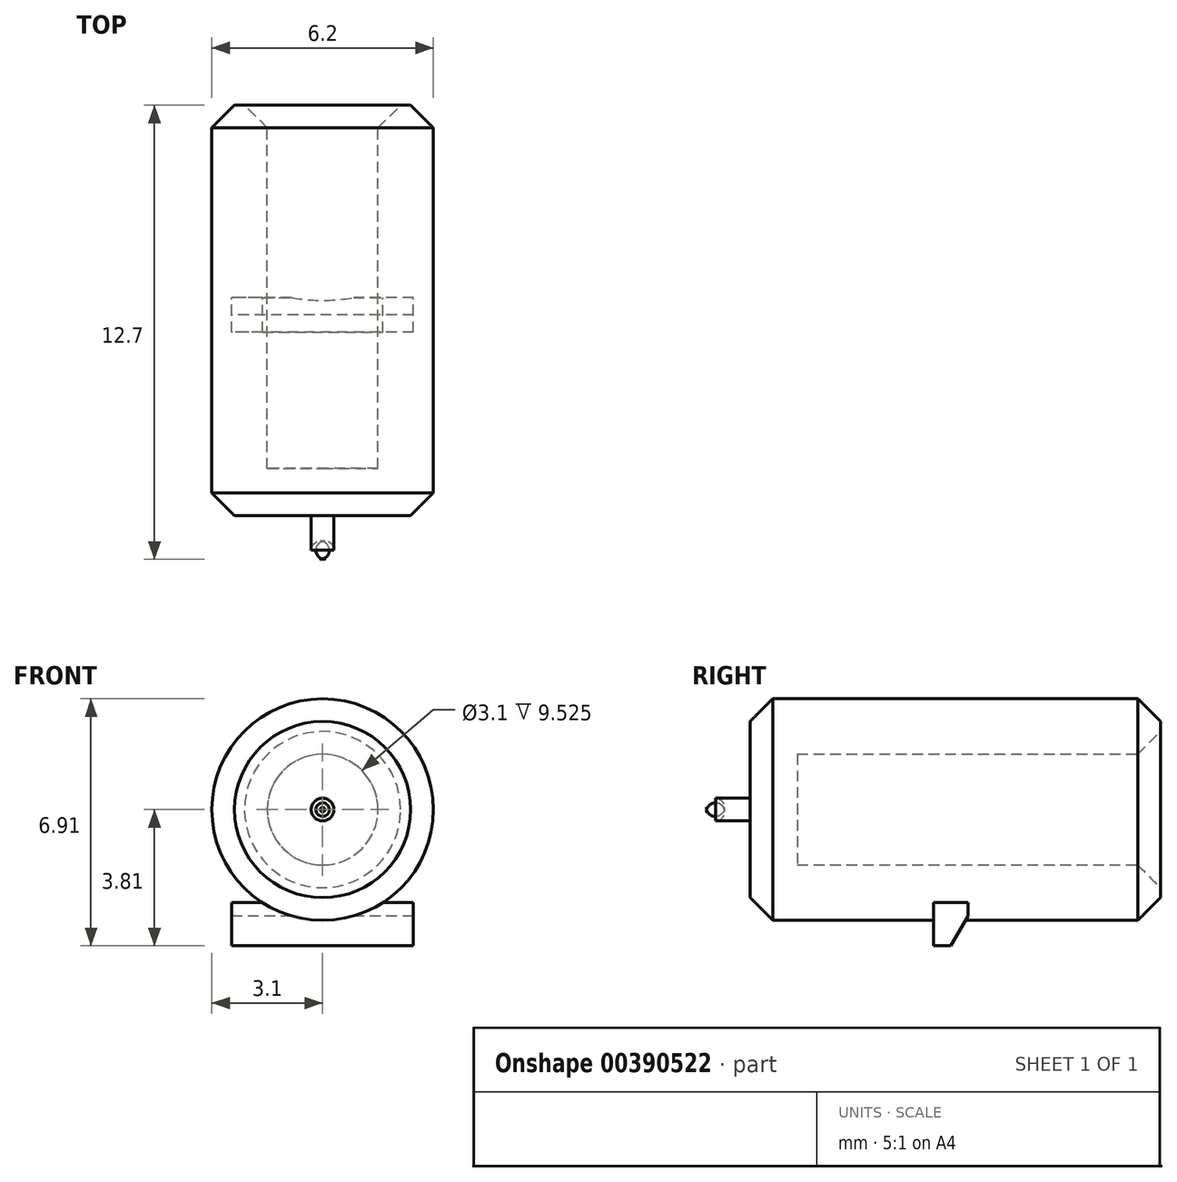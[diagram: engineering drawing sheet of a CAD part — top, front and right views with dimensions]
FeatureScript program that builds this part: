
annotation { "Feature Type Name" : "Feature", "Feature Type Description" : "" }
export const myFeature = defineFeature(function(context is Context, id is Id, definition is map)
    precondition{}
    {
        {
            var Q0;
            Q0=qCreatedBy(makeId("Right.planeOp"),FACE);
            var sketch = newSketch(context, id + "F0", { "sketchPlane" : qUnion([Q0])});
            skLineSegment(sketch, "E0", {"start": v(0, 0) * mm, "end": v(0, 0.32) * mm});
            skLineSegment(sketch, "E1", {"start": v(0, 0.32) * mm, "end": v(1.22, 0.32) * mm});
            skLineSegment(sketch, "E2", {"start": v(1.22, 0.32) * mm, "end": v(1.22, 3.1) * mm});
            skLineSegment(sketch, "E3", {"start": v(1.22, 3.1) * mm, "end": v(12.7, 3.1) * mm});
            skLineSegment(sketch, "E4", {"start": v(12.7, 3.1) * mm, "end": v(12.7, 1.55) * mm});
            skLineSegment(sketch, "E5", {"start": v(2.54, 0) * mm, "end": v(0, 0) * mm});
            skLineSegment(sketch, "E6", {"start": v(12.7, 1.55) * mm, "end": v(2.54, 1.55) * mm});
            skLineSegment(sketch, "E7", {"start": v(2.54, 1.55) * mm, "end": v(2.54, 0) * mm});
            skPoint(sketch, "E8.orphan", {"position": v(12.7, 0) * mm});
            skSolve(sketch);
        }
        {
            var Q0;
            Q0=makeQuery(id+"F0.imprint","IMPRINT",FACE,{"disambiguationData":[TD([[makeQuery(id+"F0.imprint","IMPRINT",EDGE,{"derivedFrom":sQuery(id+"F0.wireOp",EDGE,"E0")}),-1.0]])]});
            var Q1;
            Q1=sQuery(id+"F0.wireOp",EDGE,"E5");
            revolve(context, id + "F1", {"entities" : qUnion([Q0]), "axis" : qUnion([Q1]), "revolveType" : RevolveType.FULL});
        }
        {
            var Q0;
            Q0=makeQuery(id+"F1.opRevolve","SWEPT_EDGE",EDGE,{"disambiguationData":[OSD([sQuery(id+"F0.wireOp",EDGE,"E2"),sQuery(id+"F0.wireOp",EDGE,"E3")])]});
            var Q1;
            Q1=makeQuery(id+"F1.opRevolve","SWEPT_EDGE",EDGE,{"disambiguationData":[OSD([sQuery(id+"F0.wireOp",EDGE,"E4"),sQuery(id+"F0.wireOp",EDGE,"E6")])]});
            var Q2;
            Q2=makeQuery(id+"F1.opRevolve","SWEPT_EDGE",EDGE,{"disambiguationData":[OSD([sQuery(id+"F0.wireOp",EDGE,"E3"),sQuery(id+"F0.wireOp",EDGE,"E4")])]});
            chamfer(context, id + "F2", {"entities" : qUnion([Q0, Q1, Q2]), "width" : 0.64 * mm, "tangentPropagation" : true});
        }
        {
            var Q0;
            Q0=makeQuery(id+"F1.opRevolve","SWEPT_EDGE",EDGE,{"disambiguationData":[OSD([sQuery(id+"F0.wireOp",EDGE,"E0"),sQuery(id+"F0.wireOp",EDGE,"E1")])]});
            fillet(context, id + "F3", {"entities" : qUnion([Q0]), "radius" : 0.25 * mm, "tangentPropagation" : true, "allowEdgeOverflow" : false});
        }
        {
            var Q0;
            Q0=qCreatedBy(makeId("Right.planeOp"),FACE);
            var sketch = newSketch(context, id + "F4", { "sketchPlane" : qUnion([Q0])});
            skLineSegment(sketch, "E9.bottom", {"start": v(6.35, -3.81) * mm, "end": v(6.83, -3.81) * mm});
            skLineSegment(sketch, "E9.top", {"start": v(6.35, -2.6) * mm, "end": v(7.32, -2.6) * mm});
            skLineSegment(sketch, "E9.left", {"start": v(6.35, -3.81) * mm, "end": v(6.35, -2.6) * mm});
            skLineSegment(sketch, "E9.right", {"start": v(7.32, -2.97) * mm, "end": v(7.32, -2.6) * mm});
            skLineSegment(sketch, "E10", {"start": v(6.83, -3.81) * mm, "end": v(7.32, -2.97) * mm});
            skPoint(sketch, "E11.orphan", {"position": v(7.32, -3.81) * mm});
            skSolve(sketch);
        }
        {
            var Q0;
            Q0 = qSketchRegion(id + "F4", true);
            extrude(context, id + "F5", {"entities" : qUnion([Q0]), "operationType" : NewBodyOperationType.ADD, "depth" : 2.54 * mm, "hasSecondDirection" : true, "secondDirectionOppositeDirection" : true, "secondDirectionDepth" : 2.54 * mm});
        }
    });
